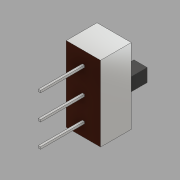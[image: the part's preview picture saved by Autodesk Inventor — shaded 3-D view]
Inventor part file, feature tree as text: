
AUTODESK INVENTOR PART (.ipt)
format: ipt  version: 2018 (Build 220112000, 112)  size: 150,016 bytes
history: native  units: mm
features: extrude x4, sketch x4
ambient origin geometry x8: Origin, YZ Plane, XZ Plane, XY Plane, X Axis, Y Axis, Z Axis, Center Point
bodies: Solid1 (feature_tree)
feature tree (8):
  extrude  "Extrusion1"  Depth=8.55mm
  extrude  "Extrusion3"  Depth=2.5mm
  extrude  "Extrusion4"  TaperAngle=90.0deg  [1 undecoded]
  extrude  "Extrusion5"  TaperAngle=0.0deg  [1 undecoded]
  sketch  "Sketch1"  dims[d0=3.9mm d1=8.55mm]
  sketch  "Sketch2"  dims[d2=3.5mm d3=0.0mm d4=2.5mm]
  sketch  "Sketch3"  dims[d5=2.5mm d6=90.0deg]
  sketch  "Sketch4"  dims[d7=1.7mm d8=0.0mm d9=1.7mm d10=180.0deg d13=0.5mm d14=0.5mm d15=180.0deg d16=0.5mm d17=0.0mm d18=0.11mm d19=0.0mm d20=1.5mm d21=1.5mm d22=3.11mm d23=0.0mm d24=1.5mm d25=90.0deg d26=0.25mm d27=0.25mm d28=1.5mm d29=90.0deg d30=0.25mm d31=0.25mm d32=3.0mm d33=90.0deg d34=0.25mm d35=0.25mm d36=5.0mm d37=0.0mm]
note: 2 required parameter values undecoded (feature->parameter linkage not recoverable at this tier; creation-order binding heuristic only, values carry confidence <= 0.55)
